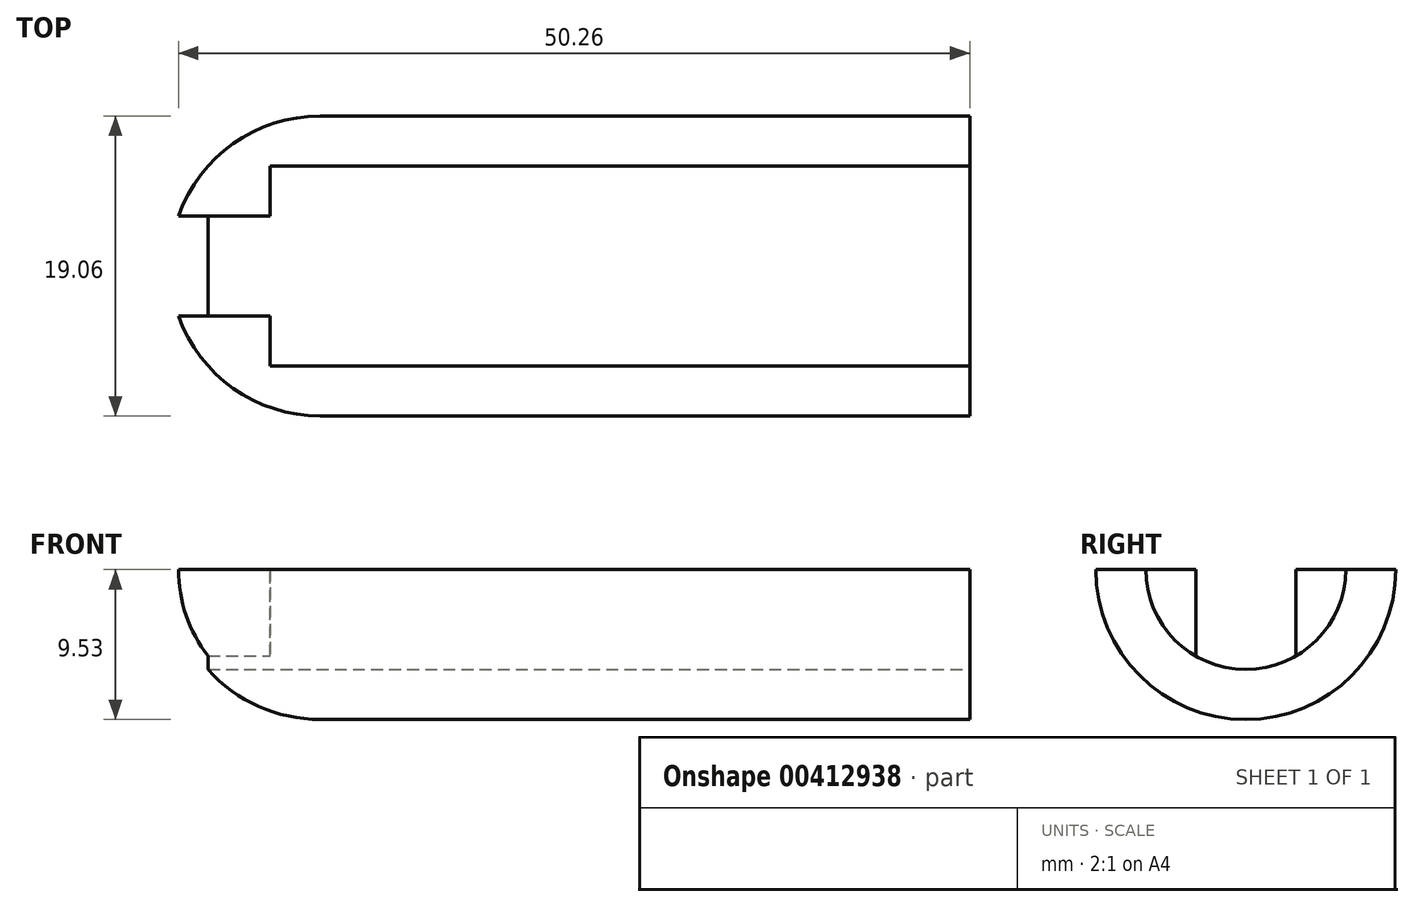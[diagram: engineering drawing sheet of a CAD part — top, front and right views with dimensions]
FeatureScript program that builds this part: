
annotation { "Feature Type Name" : "Feature", "Feature Type Description" : "" }
export const myFeature = defineFeature(function(context is Context, id is Id, definition is map)
    precondition{}
    {
        {
            var Q0;
            Q0=qCreatedBy(makeId("Right.planeOp"),FACE);
            var sketch = newSketch(context, id + "F0", { "sketchPlane" : qUnion([Q0])});
            skArc(sketch, "E0", {"start": v(-9.52, 0) * mm, "mid": v(0, -9.52) * mm, "end": v(9.52, 0) * mm});
            skLineSegment(sketch, "E1", {"start": v(9.52, 0) * mm, "end": v(-9.52, 0) * mm});
            skSolve(sketch);
        }
        {
            var Q0;
            Q0=makeQuery(id+"F0.imprint","IMPRINT",FACE,{"disambiguationData":[TD([[makeQuery(id+"F0.imprint","IMPRINT",EDGE,{"derivedFrom":sQuery(id+"F0.wireOp",EDGE,"E0")}),1.0]])]});
            extrude(context, id + "F1", {"entities" : qUnion([Q0]), "depth" : 50.8 * mm});
        }
        {
            var Q0;
            Q0=makeQuery(id+"F1.opExtrude","CAP_EDGE",EDGE,{"disambiguationData":[OSD([sQuery(id+"F0.wireOp",EDGE,"E0")])],"isStart":true});
            fillet(context, id + "F2", {"entities" : qUnion([Q0]), "radius" : 9.52 * mm, "tangentPropagation" : true, "allowEdgeOverflow" : false});
        }
        {
            var Q0;
            Q0=makeQuery(id+"F1.opExtrude","CAP_FACE",FACE,{"disambiguationData":[OSD([sQuery(id+"F0.wireOp",EDGE,"E0"),sQuery(id+"F0.wireOp",EDGE,"E1")])],"isStart":false});
            var sketch = newSketch(context, id + "F3", { "sketchPlane" : qUnion([Q0])});
            skArc(sketch, "E2", {"start": v(-9.52, 0) * mm, "mid": v(0, -9.52) * mm, "end": v(9.52, 0) * mm, "construction": true});
            skLineSegment(sketch, "E3", {"start": v(-6.35, 0) * mm, "end": v(6.35, 0) * mm});
            skArc(sketch, "E4.0", {"start": v(-6.35, 0) * mm, "mid": v(0, -6.35) * mm, "end": v(6.35, 0) * mm});
            skLineSegment(sketch, "E5", {"start": v(-9.52, 0) * mm, "end": v(-6.35, 0) * mm, "construction": true});
            skLineSegment(sketch, "E6", {"start": v(6.35, 0) * mm, "end": v(9.52, 0) * mm, "construction": true});
            skSolve(sketch);
        }
        {
            var Q0;
            Q0=makeQuery(id+"F3.imprint","IMPRINT",FACE,{"disambiguationData":[TD([[makeQuery(id+"F3.imprint","IMPRINT",EDGE,{"derivedFrom":sQuery(id+"F3.wireOp",EDGE,"E3")}),1.0]])]});
            extrude(context, id + "F4", {"entities" : qUnion([Q0]), "operationType" : NewBodyOperationType.REMOVE, "oppositeDirection" : true, "depth" : 44.45 * mm});
        }
        {
            var Q0;
            Q0=makeQuery(id+"F4.boolean.opBoolean","COPY",FACE,{"derivedFrom":makeQuery(id+"F4.opExtrude","CAP_FACE",FACE,{"disambiguationData":[OSD([sQuery(id+"F3.wireOp",EDGE,"E3"),sQuery(id+"F3.wireOp",EDGE,"E4.0")])],"isStart":false})});
            var sketch = newSketch(context, id + "F5", { "sketchPlane" : qUnion([Q0])});
            skLineSegment(sketch, "E7", {"start": v(-3.18, 0) * mm, "end": v(3.18, 0) * mm});
            skArc(sketch, "E8", {"start": v(-3.18, -5.5) * mm, "mid": v(0, -6.35) * mm, "end": v(3.17, -5.5) * mm});
            skLineSegment(sketch, "E9", {"start": v(-3.18, 0) * mm, "end": v(-3.18, -5.5) * mm});
            skLineSegment(sketch, "E10", {"start": v(3.18, 0) * mm, "end": v(3.18, -5.5) * mm});
            skSolve(sketch);
        }
        {
            var Q0;
            Q0=makeQuery(id+"F5.imprint","IMPRINT",FACE,{"disambiguationData":[TD([[makeQuery(id+"F5.imprint","IMPRINT",EDGE,{"derivedFrom":sQuery(id+"F5.wireOp",EDGE,"E7")}),1.0]])]});
            extrude(context, id + "F6", {"entities" : qUnion([Q0]), "operationType" : NewBodyOperationType.REMOVE, "oppositeDirection" : true, "depth" : 6.35 * mm});
        }
    });
